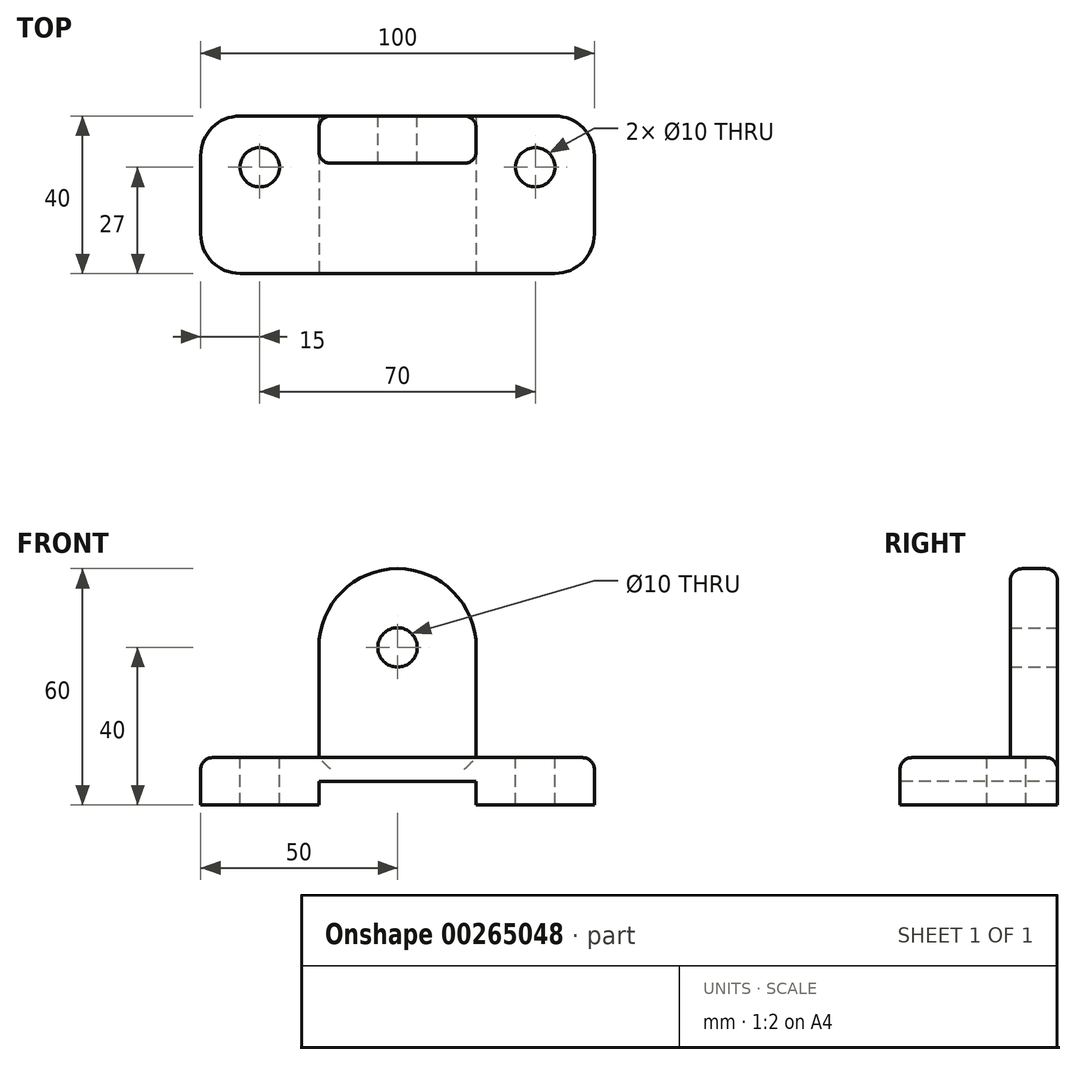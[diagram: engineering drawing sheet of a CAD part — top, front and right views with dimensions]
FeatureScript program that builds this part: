
annotation { "Feature Type Name" : "Feature", "Feature Type Description" : "" }
export const myFeature = defineFeature(function(context is Context, id is Id, definition is map)
    precondition{}
    {
        {
            var Q0;
            Q0=qCreatedBy(makeId("Top.planeOp"),FACE);
            var sketch = newSketch(context, id + "F0", { "sketchPlane" : qUnion([Q0])});
            skLineSegment(sketch, "E0.bottom", {"start": v(-40, 20) * mm, "end": v(40, 20) * mm});
            skLineSegment(sketch, "E0.top", {"start": v(-40, -20) * mm, "end": v(40, -20) * mm});
            skLineSegment(sketch, "E0.left", {"start": v(-50, 10) * mm, "end": v(-50, -10) * mm});
            skLineSegment(sketch, "E0.right", {"start": v(50, 10) * mm, "end": v(50, -10) * mm});
            skPoint(sketch, "E1.visualSharp", {"position": v(-50, 20) * mm});
            skArc(sketch, "E1.filletArc", {"start": v(-40, 20) * mm, "mid": v(-47.07, 17.07) * mm, "end": v(-50, 10) * mm});
            skPoint(sketch, "E2.visualSharp", {"position": v(-50, -20) * mm});
            skArc(sketch, "E2.filletArc", {"start": v(-50, -10) * mm, "mid": v(-47.07, -17.07) * mm, "end": v(-40, -20) * mm});
            skPoint(sketch, "E3.visualSharp", {"position": v(50, -20) * mm});
            skArc(sketch, "E3.filletArc", {"start": v(40, -20) * mm, "mid": v(47.07, -17.07) * mm, "end": v(50, -10) * mm});
            skPoint(sketch, "E4.visualSharp", {"position": v(50, 20) * mm});
            skArc(sketch, "E4.filletArc", {"start": v(50, 10) * mm, "mid": v(47.07, 17.07) * mm, "end": v(40, 20) * mm});
            skSolve(sketch);
        }
        {
            var Q0;
            Q0 = qSketchRegion(id + "F0", true);
            extrude(context, id + "F1", {"entities" : qUnion([Q0]), "depth" : 12 * mm});
        }
        {
            var Q0;
            Q0=makeQuery(id+"F1.opExtrude","CAP_FACE",FACE,{"disambiguationData":[OSD([sQuery(id+"F0.wireOp",EDGE,"E0.bottom"),sQuery(id+"F0.wireOp",EDGE,"E0.top"),sQuery(id+"F0.wireOp",EDGE,"E0.left"),sQuery(id+"F0.wireOp",EDGE,"E0.right"),sQuery(id+"F0.wireOp",EDGE,"E1.filletArc"),sQuery(id+"F0.wireOp",EDGE,"E2.filletArc"),sQuery(id+"F0.wireOp",EDGE,"E3.filletArc"),sQuery(id+"F0.wireOp",EDGE,"E4.filletArc")])],"isStart":true});
            var sketch = newSketch(context, id + "F2", { "sketchPlane" : qUnion([Q0])});
            skLineSegment(sketch, "E5.bottom", {"start": v(-20, -20) * mm, "end": v(20, -20) * mm});
            skLineSegment(sketch, "E5.top", {"start": v(-20, 20) * mm, "end": v(20, 20) * mm});
            skLineSegment(sketch, "E5.left", {"start": v(-20, -20) * mm, "end": v(-20, 20) * mm});
            skLineSegment(sketch, "E5.right", {"start": v(20, -20) * mm, "end": v(20, 20) * mm});
            skSolve(sketch);
        }
        {
            var Q0;
            Q0 = qSketchRegion(id + "F2", true);
            extrude(context, id + "F3", {"entities" : qUnion([Q0]), "operationType" : NewBodyOperationType.REMOVE, "oppositeDirection" : true, "depth" : 6 * mm});
        }
        {
            var Q0;
            Q0=makeQuery(id+"F1.opExtrude","CAP_FACE",FACE,{"disambiguationData":[OSD([sQuery(id+"F0.wireOp",EDGE,"E0.bottom"),sQuery(id+"F0.wireOp",EDGE,"E0.top"),sQuery(id+"F0.wireOp",EDGE,"E0.left"),sQuery(id+"F0.wireOp",EDGE,"E0.right"),sQuery(id+"F0.wireOp",EDGE,"E1.filletArc"),sQuery(id+"F0.wireOp",EDGE,"E2.filletArc"),sQuery(id+"F0.wireOp",EDGE,"E3.filletArc"),sQuery(id+"F0.wireOp",EDGE,"E4.filletArc")])],"isStart":false});
            var sketch = newSketch(context, id + "F4", { "sketchPlane" : qUnion([Q0])});
            skCircle(sketch, "E6", {"center": v(-35, 7) * mm, "radius": 5 * mm});
            skCircle(sketch, "E7.MirrorC", {"center": v(35, 7) * mm, "radius": 5 * mm});
            skSolve(sketch);
        }
        {
            var Q0;
            Q0 = qSketchRegion(id + "F4", true);
            extrude(context, id + "F5", {"entities" : qUnion([Q0]), "operationType" : NewBodyOperationType.REMOVE, "oppositeDirection" : true, "depth" : 25 * mm});
        }
        {
            var Q0;
            Q0=makeQuery(id+"F1.opExtrude","SWEPT_FACE",FACE,{"disambiguationData":[OSD([sQuery(id+"F0.wireOp",EDGE,"E0.bottom")])]});
            var sketch = newSketch(context, id + "F6", { "sketchPlane" : qUnion([Q0])});
            skLineSegment(sketch, "E8.bottom", {"start": v(20, 12) * mm, "end": v(-20, 12) * mm});
            skLineSegment(sketch, "E8.top", {"start": v(0, 60) * mm, "end": v(0, 60) * mm});
            skLineSegment(sketch, "E8.left", {"start": v(20, 12) * mm, "end": v(20, 40) * mm});
            skLineSegment(sketch, "E8.right", {"start": v(-20, 12) * mm, "end": v(-20, 40) * mm});
            skPoint(sketch, "E9.visualSharp", {"position": v(20, 60) * mm});
            skArc(sketch, "E9.filletArc", {"start": v(20, 40) * mm, "mid": v(14.14, 54.14) * mm, "end": v(0, 60) * mm});
            skPoint(sketch, "E10.visualSharp", {"position": v(-20, 60) * mm});
            skArc(sketch, "E10.filletArc", {"start": v(0, 60) * mm, "mid": v(-14.14, 54.14) * mm, "end": v(-20, 40) * mm});
            skCircle(sketch, "E11", {"center": v(0, 40) * mm, "radius": 5 * mm});
            skSolve(sketch);
        }
        {
            var Q0;
            Q0 = qSketchRegion(id + "F6", true);
            extrude(context, id + "F7", {"entities" : qUnion([Q0]), "oppositeDirection" : true, "depth" : 12 * mm});
        }
        {
            var Q0;
            Q0=makeQuery(id+"F7.opExtrude","SWEPT_BODY",BODY,{"disambiguationData":[OSD([sQuery(id+"F6.wireOp",EDGE,"E8.bottom"),sQuery(id+"F6.wireOp",EDGE,"E8.left"),sQuery(id+"F6.wireOp",EDGE,"E8.right"),sQuery(id+"F6.wireOp",EDGE,"E9.filletArc"),sQuery(id+"F6.wireOp",EDGE,"E10.filletArc"),sQuery(id+"F6.wireOp",EDGE,"E11")])]});
            var Q1;
            Q1=makeQuery(id+"F1.opExtrude","SWEPT_BODY",BODY,{"disambiguationData":[OSD([sQuery(id+"F0.wireOp",EDGE,"E0.bottom"),sQuery(id+"F0.wireOp",EDGE,"E0.top"),sQuery(id+"F0.wireOp",EDGE,"E0.left"),sQuery(id+"F0.wireOp",EDGE,"E0.right"),sQuery(id+"F0.wireOp",EDGE,"E1.filletArc"),sQuery(id+"F0.wireOp",EDGE,"E2.filletArc"),sQuery(id+"F0.wireOp",EDGE,"E3.filletArc"),sQuery(id+"F0.wireOp",EDGE,"E4.filletArc")])]});
            booleanBodies(context, id + "F8", {"operationType" : BooleanOperationType.UNION, "tools" : qUnion([Q0, Q1])});
        }
        {
            var Q0;
            Q0=makeQuery(id+"F7.opExtrude","CAP_EDGE",EDGE,{"disambiguationData":[OSD([sQuery(id+"F6.wireOp",EDGE,"E8.left")])],"isStart":true});
            var Q1;
            Q1=makeQuery(id+"F7.opExtrude","SWEPT_EDGE",EDGE,{"disambiguationData":[OSD([sQuery(id+"F0.wireOp",EDGE,"E0.bottom"),sQuery(id+"F6.wireOp",EDGE,"E8.bottom"),sQuery(id+"F6.wireOp",EDGE,"E8.left")])]});
            var Q2;
            {var subQ0=sQuery(id+"F0.wireOp",EDGE,"E1.filletArc");var subQ2=sQuery(id+"F0.wireOp",EDGE,"E0.bottom");Q2=makeQuery(id+"F8.opBoolean","SPLIT",EDGE,{"disambiguationData":[TD([makeQuery(id+"F1.opExtrude","SWEPT_FACE",FACE,{"disambiguationData":[OSD([subQ0])]})])],"derivedFrom":makeQuery(id+"F1.opExtrude","CAP_EDGE",EDGE,{"disambiguationData":[OSD([subQ2])],"isStart":false})});}
            var Q3;
            Q3=makeQuery(id+"F7.opExtrude","CAP_EDGE",EDGE,{"disambiguationData":[OSD([sQuery(id+"F6.wireOp",EDGE,"E8.bottom")])],"isStart":false});
            var Q4;
            Q4=makeQuery(id+"F7.opExtrude","CAP_EDGE",EDGE,{"disambiguationData":[OSD([sQuery(id+"F6.wireOp",EDGE,"E8.right")])],"isStart":false});
            var Q5;
            Q5=makeQuery(id+"F7.opExtrude","SWEPT_EDGE",EDGE,{"disambiguationData":[OSD([sQuery(id+"F0.wireOp",EDGE,"E0.bottom"),sQuery(id+"F6.wireOp",EDGE,"E8.bottom"),sQuery(id+"F6.wireOp",EDGE,"E8.right")])]});
            fillet(context, id + "F9", {"entities" : qUnion([Q0, Q1, Q2, Q3, Q4, Q5]), "radius" : 3 * mm, "tangentPropagation" : true, "allowEdgeOverflow" : false});
        }
    });
